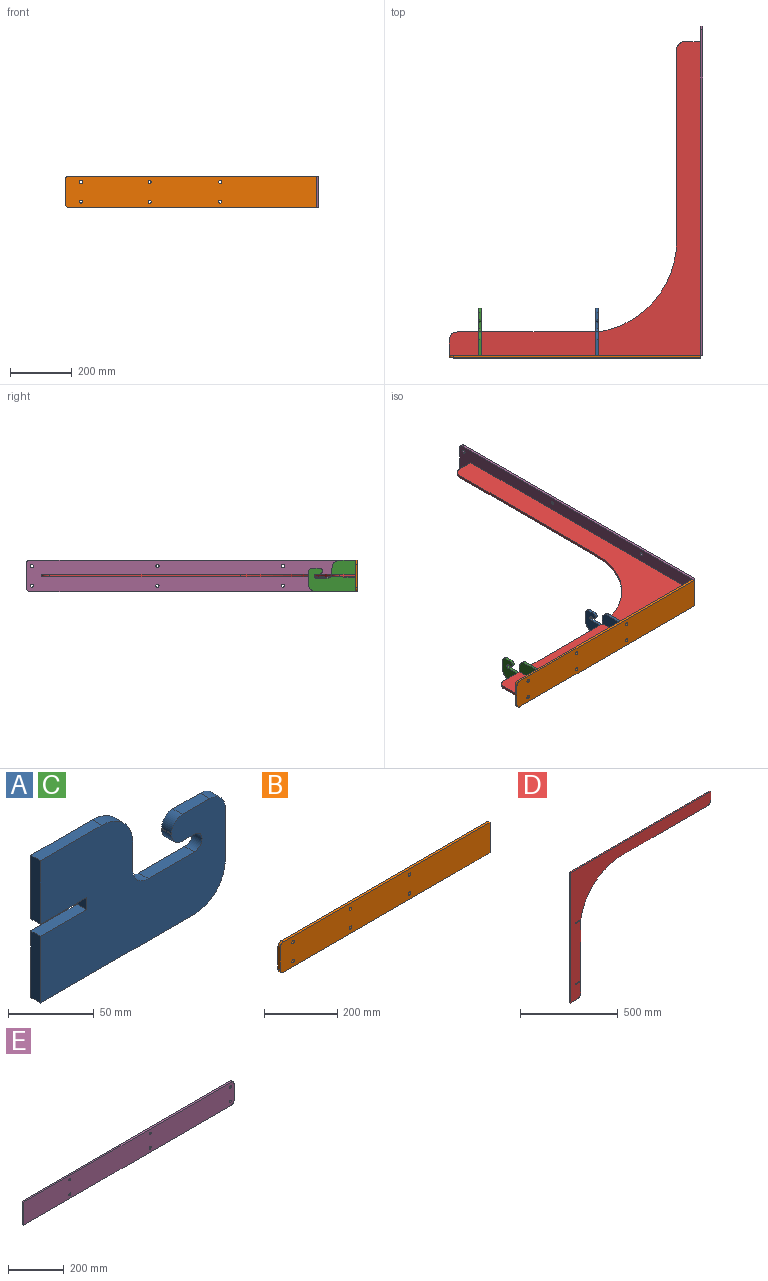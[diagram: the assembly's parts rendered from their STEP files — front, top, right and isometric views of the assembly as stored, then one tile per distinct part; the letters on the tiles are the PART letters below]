
ASSEMBLY  parts=5 mates=13
PART A: 22 faces, bbox 152.4x7.9x101.6 mm
  f0: plane 19.05x7.92mm, normal (1,0,0), area 151mm2, adj f13,f14,f19,f20
  f1: plane 50.8x7.92mm, normal (0,0,1), area 402.6mm2, adj f2,f13,f14,f20
  f2: plane 45.37x7.92mm, normal (-1,0,0), area 359.6mm2, adj f1,f3,f13,f14
  f3: plane 38.1x7.92mm, normal (0,0,-1), area 301.9mm2, adj f2,f4,f13,f14
  f4: plane 8.64x7.92mm, normal (-1,0,0), area 68.4mm2, adj f3,f5,f13,f14
  f5: plane 38.1x7.92mm, normal (0,0,1), area 301.9mm2, adj f4,f6,f13,f14
  f6: plane 47.59x7.92mm, normal (-1,0,0), area 377.1mm2, adj f5,f7,f13,f14
  f7: plane 127x7.92mm, normal (0,0,-1), area 1006.4mm2, adj f6,f13,f14,f21
  f8: plane 38.1x7.92mm, normal (1,0,0), area 301.9mm2, adj f13,f14,f17,f21
  f9: plane 22.55x7.92mm, normal (0,0,1), area 178.7mm2, adj f13,f14,f15,f17
  f10: plane 7.92x0.65mm, normal (-1,0,0), area 5.2mm2, adj f13,f14,f15,f16
  f11: plane 9.85x7.92mm, normal (0,0,-1), area 78.1mm2, adj f13,f14,f16,f18
  f12: plane 38.1x7.92mm, normal (0,0,1), area 301.9mm2, adj f13,f14,f18,f19
  f13: plane 152.4x101.6mm, normal (0,-1,0), area 11592.8mm2, adj f0,f1,f2,f3,f4,f5,f6,f7
  f14: plane 152.4x101.6mm, normal (0,1,0), area 11592.8mm2, adj f0,f1,f2,f3,f4,f5,f6,f7
  f15: cylinder r=9.2mm len=9.2mm, axis (0,1,0), area 114.5mm2, adj f9,f10,f13,f14
  f16: cylinder r=9.2mm len=9.2mm, axis (0,1,0), area 114.5mm2, adj f10,f11,f13,f14
  f17: cylinder r=12.7mm len=12.7mm, axis (0,-1,0), area 158.1mm2, adj f8,f9,f13,f14
  f18: cylinder r=6.35mm len=12.7mm, axis (0,1,0), area 158.1mm2, adj f11,f12,f13,f14
  f19: cylinder r=12.7mm len=12.7mm, axis (0,-1,0), area 158.1mm2, adj f0,f12,f13,f14
  f20: cylinder r=25.4mm len=25.4mm, axis (0,1,0), area 316.2mm2, adj f0,f1,f13,f14
  f21: cylinder r=25.4mm len=25.4mm, axis (0,-1,0), area 316.2mm2, adj f7,f8,f13,f14
PART B: 14 faces, bbox 812.8x7.9x101.6 mm
  f0: plane 800.1x7.92mm, normal (0,0,-1), area 6340.6mm2, adj f1,f10,f11,f13
  f1: plane 101.6x7.92mm, normal (1,0,0), area 805.2mm2, adj f0,f2,f10,f11
  f2: plane 800.1x7.92mm, normal (0,0,1), area 6340.6mm2, adj f1,f10,f11,f12
  f3: cylinder r=5.08mm len=10.16mm, axis (0,1,0), area 252.9mm2, adj f10,f11
  f4: cylinder r=5.08mm len=10.16mm, axis (0,1,0), area 252.9mm2, adj f10,f11
  f5: cylinder r=5.08mm len=10.16mm, axis (0,1,0), area 252.9mm2, adj f10,f11
  f6: cylinder r=5.08mm len=10.16mm, axis (0,1,0), area 252.9mm2, adj f10,f11
  f7: cylinder r=5.08mm len=10.16mm, axis (0,1,0), area 252.9mm2, adj f10,f11
  f8: cylinder r=5.08mm len=10.16mm, axis (0,1,0), area 252.9mm2, adj f10,f11
  f9: plane 76.2x7.92mm, normal (-1,0,0), area 603.9mm2, adj f10,f11,f12,f13
  f10: plane 812.8x101.6mm, normal (0,-1,0), area 82024.8mm2, adj f0,f1,f2,f3,f4,f5,f6,f7
  f11: plane 812.8x101.6mm, normal (0,1,0), area 82024.8mm2, adj f0,f1,f2,f3,f4,f5,f6,f7
  f12: cylinder r=12.7mm len=12.7mm, axis (0,-1,0), area 158.1mm2, adj f2,f9,f10,f11
  f13: cylinder r=12.7mm len=12.7mm, axis (0,1,0), area 158.1mm2, adj f0,f9,f10,f11
PART C: same geometry as A
PART D: 18 faces, bbox 1016x7.9x812.8 mm
  f0: plane 40.64x7.92mm, normal (0,0,-1), area 322.1mm2, adj f12,f13,f14,f16
  f1: plane 618.11x7.92mm, normal (0,0,-1), area 4898.4mm2, adj f13,f14,f15,f16
  f2: plane 50.8x7.92mm, normal (1,0,0), area 402.6mm2, adj f3,f13,f14,f15
  f3: plane 1016x7.92mm, normal (0,0,1), area 8051.6mm2, adj f2,f4,f13,f14
  f4: plane 812.8x7.92mm, normal (-1,0,0), area 6441.3mm2, adj f3,f5,f13,f14
  f5: plane 50.8x7.92mm, normal (0,0,-1), area 402.6mm2, adj f4,f13,f14,f17
  f6: plane 69.85x7.92mm, normal (1,0,0), area 553.5mm2, adj f7,f13,f14,f17
  f7: plane 40.64x7.92mm, normal (0,0,1), area 322.1mm2, adj f6,f8,f13,f14
  f8: plane 7.92x6.6mm, normal (1,0,0), area 52.3mm2, adj f7,f9,f13,f14
  f9: plane 40.64x7.92mm, normal (0,0,-1), area 322.1mm2, adj f8,f10,f13,f14
  f10: plane 374.4x7.92mm, normal (1,0,0), area 2967mm2, adj f9,f11,f13,f14
  f11: plane 40.64x7.92mm, normal (0,0,1), area 322.1mm2, adj f10,f12,f13,f14
  f12: plane 7.92x6.6mm, normal (1,0,0), area 52.3mm2, adj f0,f11,f13,f14
  f13: plane 1016x812.8mm, normal (0,-1,0), area 151070.7mm2, adj f0,f1,f2,f3,f4,f5,f6,f7
  f14: plane 1016x812.8mm, normal (0,1,0), area 151070.7mm2, adj f0,f1,f2,f3,f4,f5,f6,f7
  f15: cylinder r=25.4mm len=25.4mm, axis (0,1,0), area 316.2mm2, adj f1,f2,f13,f14
  f16: cylinder r=299.86mm len=296.29mm, axis (0,-1,0), area 3365.8mm2, adj f0,f1,f13,f14
  f17: cylinder r=25.4mm len=25.4mm, axis (0,-1,0), area 316.2mm2, adj f5,f6,f13,f14
PART E: 14 faces, bbox 1066.8x7.9x101.6 mm
  f0: plane 1054.1x7.92mm, normal (0,0,-1), area 8353.5mm2, adj f9,f10,f11,f12
  f1: plane 76.2x7.92mm, normal (1,0,0), area 603.9mm2, adj f10,f11,f12,f13
  f2: plane 1054.1x7.92mm, normal (0,0,1), area 8353.5mm2, adj f9,f10,f11,f13
  f3: cylinder r=5.14mm len=10.29mm, axis (0,1,0), area 256.1mm2, adj f10,f11
  f4: cylinder r=5.14mm len=10.29mm, axis (0,1,0), area 256.1mm2, adj f10,f11
  f5: cylinder r=5.14mm len=10.29mm, axis (0,1,0), area 256.1mm2, adj f10,f11
  f6: cylinder r=5.14mm len=10.29mm, axis (0,1,0), area 256.1mm2, adj f10,f11
  f7: cylinder r=5.14mm len=10.29mm, axis (0,1,0), area 256.1mm2, adj f10,f11
  f8: cylinder r=5.14mm len=10.29mm, axis (0,1,0), area 256.1mm2, adj f10,f11
  f9: plane 101.6x7.92mm, normal (-1,0,0), area 805.2mm2, adj f0,f2,f10,f11
  f10: plane 1066.8x101.6mm, normal (0,-1,0), area 107819mm2, adj f0,f1,f2,f3,f4,f5,f6,f7
  f11: plane 1066.8x101.6mm, normal (0,1,0), area 107819mm2, adj f0,f1,f2,f3,f4,f5,f6,f7
  f12: cylinder r=12.7mm len=12.7mm, axis (0,-1,0), area 158.1mm2, adj f0,f1,f10,f11
  f13: cylinder r=12.7mm len=12.7mm, axis (0,1,0), area 158.1mm2, adj f1,f2,f10,f11
PLACE A rot(axis=(0,0,1),90deg) t=(-138.19,396.75,338.98)mm
PLACE B rot(axis=(-0.12,-0.99,0),0deg) t=(199.68,244.35,338.98)mm
PLACE C rot(axis=(0,0,1),90deg) t=(-517.87,396.75,338.27)mm
PLACE D rot(axis=(0.58,0.58,0.58),120deg) t=(-613.12,1260.35,394.5)mm
PLACE E rot(axis=(-0.71,-0.71,0),180deg) t=(207.61,1311.15,440.58)mm
MATE planar E.f10 <-> D.f3  axis (-1,0,0) through (199.68,776.91,389.78)mm
MATE planar C.f3 <-> D.f14  axis (0,0,-1) through (-513.9,263.4,394.5)mm
MATE planar B.f1 <-> D.f3  axis (1,0,0) through (199.68,240.39,389.78)mm
MATE planar E.f2 <-> B.f0  axis (0,0,-1) through (203.65,771.4,338.98)mm
MATE planar A.f1 <-> B.f2  axis (0,0,1) through (-134.22,269.75,440.58)mm
MATE planar D.f4 <-> B.f11  axis (0,-1,0) through (-206.72,244.35,390.53)mm
MATE planar A.f13 <-> D.f0  axis (1,0,0) through (-130.26,312.19,382.43)mm
MATE planar A.f5 <-> D.f13  axis (0,0,1) through (-134.22,263.4,386.57)mm
MATE planar C.f20 <-> D.f7  axis (-1,0,0) through (-517.87,295.15,414.47)mm
MATE planar A.f2 <-> D.f4  axis (0,-1,0) through (-134.22,244.35,417.89)mm
MATE planar C.f6 <-> D.f4  axis (0,-1,0) through (-513.9,244.35,362.07)mm
MATE planar D.f3 <-> E.f10  axis (1,0,0) through (199.68,752.35,390.53)mm
MATE planar E.f9 <-> D.f4  axis (0,-1,0) through (199.68,244.35,389.78)mm
